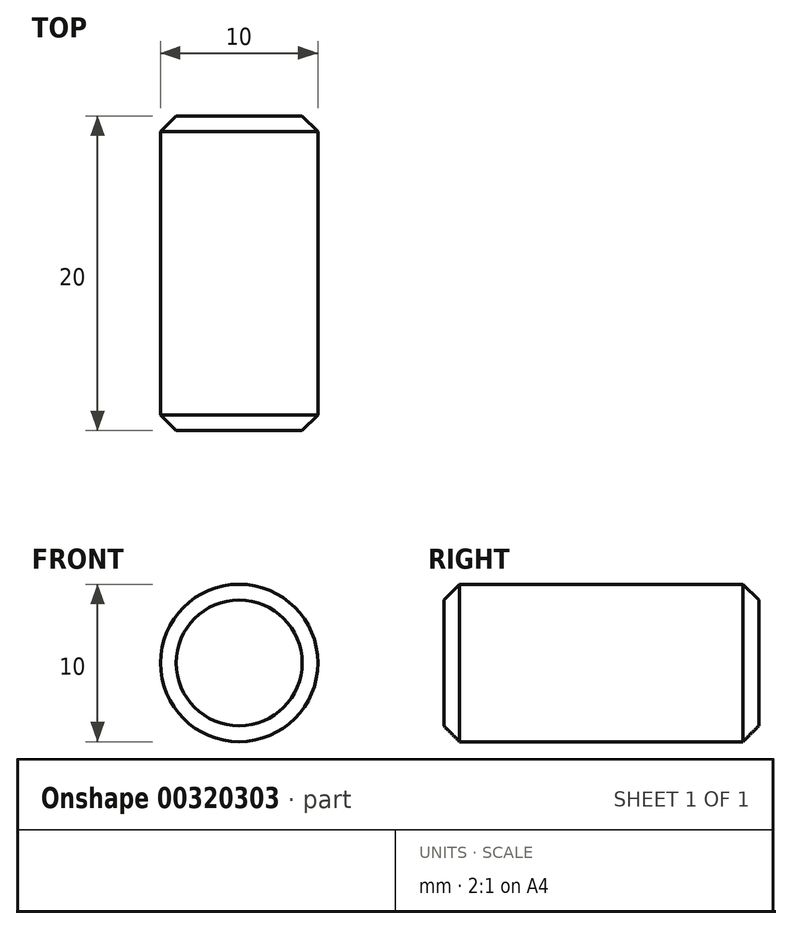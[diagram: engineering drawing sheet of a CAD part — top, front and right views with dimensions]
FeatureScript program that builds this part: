
annotation { "Feature Type Name" : "Feature", "Feature Type Description" : "" }
export const myFeature = defineFeature(function(context is Context, id is Id, definition is map)
    precondition{}
    {
        {
            var Q0;
            Q0=qCreatedBy(makeId("Front.planeOp"),FACE);
            var sketch = newSketch(context, id + "F0", { "sketchPlane" : qUnion([Q0])});
            skCircle(sketch, "E0", {"center": v(0, 0) * mm, "radius": 5 * mm});
            skSolve(sketch);
        }
        {
            var Q0;
            Q0=makeQuery(id+"F0.imprint","IMPRINT",FACE,{"disambiguationData":[TD([[makeQuery(id+"F0.imprint","IMPRINT",EDGE,{"derivedFrom":sQuery(id+"F0.wireOp",EDGE,"E0")}),1.0]])]});
            extrude(context, id + "F1", {"entities" : qUnion([Q0]), "depth" : 20 * mm});
        }
        {
            var Q0;
            Q0=makeQuery(id+"F1.opExtrude","CAP_EDGE",EDGE,{"disambiguationData":[OSD([sQuery(id+"F0.wireOp",EDGE,"E0")])],"isStart":true});
            chamfer(context, id + "F2", {"entities" : qUnion([Q0]), "width" : 1 * mm, "tangentPropagation" : true});
        }
        {
            var Q0;
            Q0=makeQuery(id+"F1.opExtrude","CAP_EDGE",EDGE,{"disambiguationData":[OSD([sQuery(id+"F0.wireOp",EDGE,"E0")])],"isStart":false});
            chamfer(context, id + "F3", {"entities" : qUnion([Q0]), "width" : 1 * mm, "tangentPropagation" : true});
        }
    });
